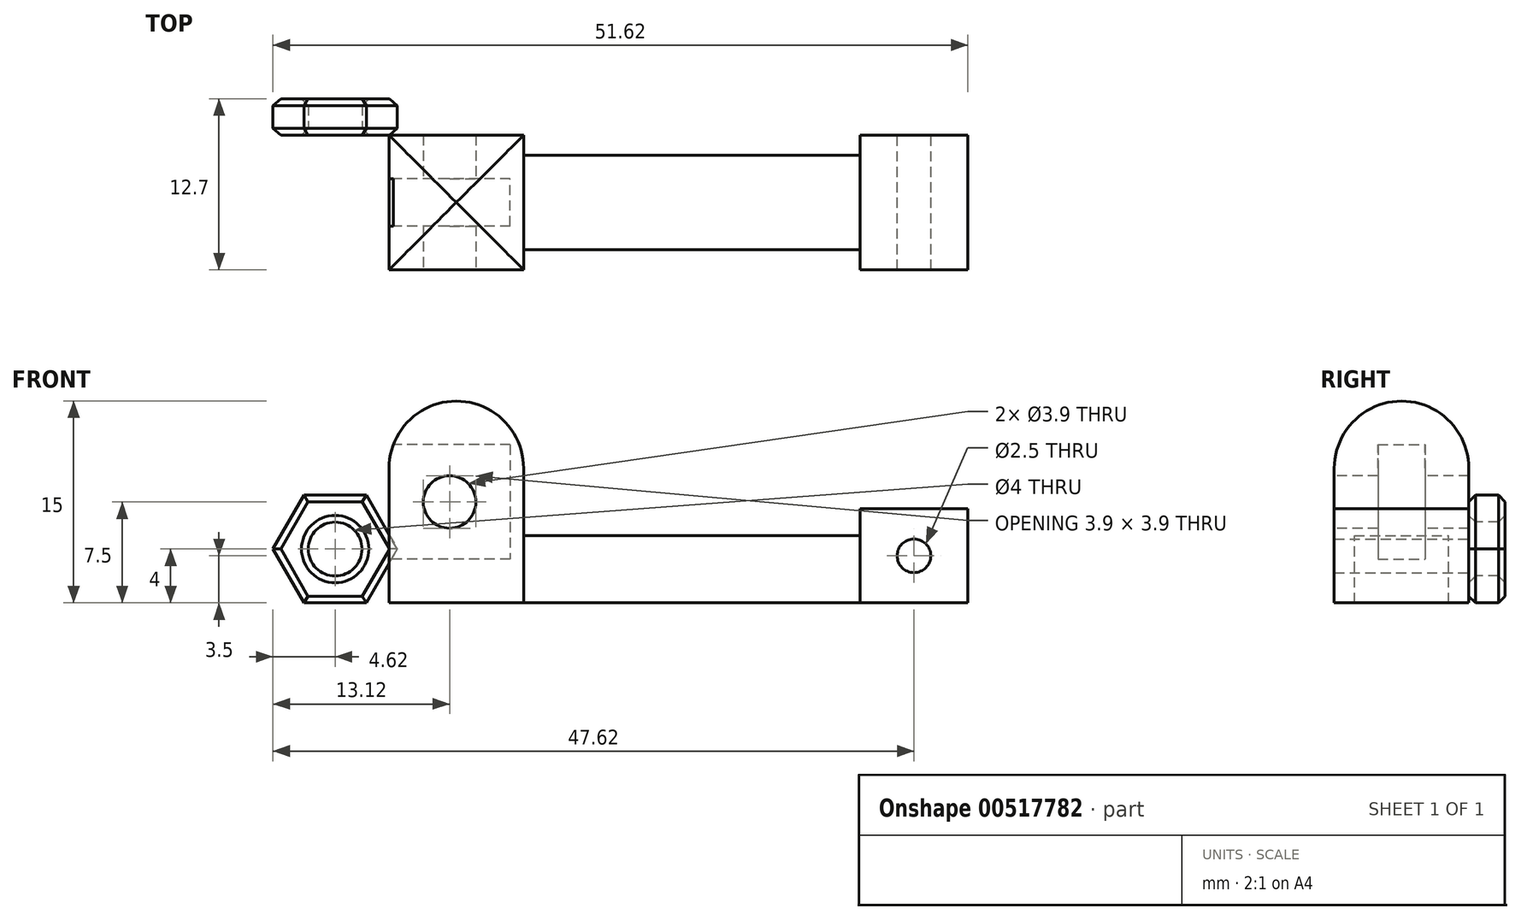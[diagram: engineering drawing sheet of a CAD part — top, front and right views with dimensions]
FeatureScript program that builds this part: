
annotation { "Feature Type Name" : "Feature", "Feature Type Description" : "" }
export const myFeature = defineFeature(function(context is Context, id is Id, definition is map)
    precondition{}
    {
        {
            var Q0;
            Q0=qCreatedBy(makeId("Front.planeOp"),FACE);
            var sketch = newSketch(context, id + "F0", { "sketchPlane" : qUnion([Q0])});
            skLineSegment(sketch, "E0.top", {"start": v(0, 15) * mm, "end": v(10, 15) * mm});
            skLineSegment(sketch, "E0.left", {"start": v(0, 0) * mm, "end": v(0, 15) * mm});
            skLineSegment(sketch, "E0.right", {"start": v(10, 5) * mm, "end": v(10, 15) * mm});
            skLineSegment(sketch, "E1.bottom", {"start": v(0, 0) * mm, "end": v(43, 0) * mm});
            skLineSegment(sketch, "E1.top", {"start": v(10, 5) * mm, "end": v(35, 5) * mm});
            skCircle(sketch, "E2", {"center": v(39, 3.5) * mm, "radius": 1.25 * mm});
            skPoint(sketch, "E3", {"position": v(35, 5) * mm});
            skLineSegment(sketch, "E4", {"start": v(35, 5) * mm, "end": v(35, 7) * mm});
            skLineSegment(sketch, "E5", {"start": v(35, 7) * mm, "end": v(43, 7) * mm});
            skLineSegment(sketch, "E6", {"start": v(43, 7) * mm, "end": v(43, 0) * mm});
            skSolve(sketch);
        }
        {
            var Q0;
            Q0 = qSketchRegion(id + "F0", true);
            extrude(context, id + "F1", {"entities" : qUnion([Q0]), "depth" : 10 * mm, "offsetDistance" : 25 * mm});
        }
        {
            var Q0;
            Q0=makeQuery(id+"F1.opExtrude","SWEPT_FACE",FACE,{"disambiguationData":[OSD([sQuery(id+"F0.wireOp",EDGE,"E0.left")])]});
            var sketch = newSketch(context, id + "F2", { "sketchPlane" : qUnion([Q0])});
            skLineSegment(sketch, "E7.bottom", {"start": v(6.75, 11.75) * mm, "end": v(3.25, 11.75) * mm});
            skLineSegment(sketch, "E7.top", {"start": v(6.75, 3.25) * mm, "end": v(3.25, 3.25) * mm});
            skLineSegment(sketch, "E7.left", {"start": v(6.75, 11.75) * mm, "end": v(6.75, 3.25) * mm});
            skLineSegment(sketch, "E7.right", {"start": v(3.25, 11.75) * mm, "end": v(3.25, 3.25) * mm});
            skPoint(sketch, "E7.middle", {"position": v(5, 7.5) * mm});
            skPoint(sketch, "E7.middle.positionSnap0", {"position": v(0, 7.5) * mm});
            skPoint(sketch, "E7.centerSnap0", {"position": v(0, 7.5) * mm});
            skSolve(sketch);
        }
        {
            var Q0;
            Q0 = qSketchRegion(id + "F2", true);
            extrude(context, id + "F3", {"entities" : qUnion([Q0]), "operationType" : NewBodyOperationType.REMOVE, "oppositeDirection" : true, "depth" : 9 * mm, "offsetDistance" : 25 * mm});
        }
        {
            var Q0;
            Q0=makeQuery(id+"F1.opExtrude","CAP_FACE",FACE,{"disambiguationData":[OSD([sQuery(id+"F0.wireOp",EDGE,"E0.top"),sQuery(id+"F0.wireOp",EDGE,"E0.left"),sQuery(id+"F0.wireOp",EDGE,"E0.right"),sQuery(id+"F0.wireOp",EDGE,"E1.bottom"),sQuery(id+"F0.wireOp",EDGE,"E1.top"),sQuery(id+"F0.wireOp",EDGE,"E1.right")])],"isStart":false});
            var sketch = newSketch(context, id + "F4", { "sketchPlane" : qUnion([Q0])});
            skCircle(sketch, "E8", {"center": v(4.5, 7.5) * mm, "radius": 1.95 * mm});
            skPoint(sketch, "E8.centerSnap0", {"position": v(0, 7.5) * mm});
            skSolve(sketch);
        }
        {
            var Q0;
            Q0 = qSketchRegion(id + "F4", true);
            var Q1;
            Q1=makeQuery(id+"F1.opExtrude","CAP_FACE",FACE,{"disambiguationData":[OSD([sQuery(id+"F0.wireOp",EDGE,"E0.top"),sQuery(id+"F0.wireOp",EDGE,"E0.left"),sQuery(id+"F0.wireOp",EDGE,"E0.right"),sQuery(id+"F0.wireOp",EDGE,"E1.bottom"),sQuery(id+"F0.wireOp",EDGE,"E1.top"),sQuery(id+"F0.wireOp",EDGE,"E1.right")])],"isStart":true});
            extrude(context, id + "F5", {"entities" : qUnion([Q0]), "operationType" : NewBodyOperationType.REMOVE, "endBound" : BoundingType.UP_TO_SURFACE, "oppositeDirection" : true, "depth" : 25 * mm, "endBoundEntityFace" : qUnion([Q1]), "offsetDistance" : 25 * mm});
        }
        {
            var Q0;
            Q0=makeQuery(id+"F1.opExtrude","SWEPT_FACE",FACE,{"disambiguationData":[OSD([sQuery(id+"F0.wireOp",EDGE,"E0.top")])]});
            fillet(context, id + "F6", {"entities" : qUnion([Q0]), "radius" : 5 * mm, "tangentPropagation" : true, "allowEdgeOverflow" : false});
        }
        {
            var Q0;
            Q0=makeQuery(id+"F1.opExtrude","SWEPT_FACE",FACE,{"disambiguationData":[OSD([sQuery(id+"F0.wireOp",EDGE,"E1.top")])]});
            var sketch = newSketch(context, id + "F7", { "sketchPlane" : qUnion([Q0])});
            skLineSegment(sketch, "E9.bottom", {"start": v(35, 0) * mm, "end": v(10, 0) * mm});
            skLineSegment(sketch, "E9.top", {"start": v(35, -1.5) * mm, "end": v(10, -1.5) * mm});
            skLineSegment(sketch, "E9.left", {"start": v(35, 0) * mm, "end": v(35, -1.5) * mm});
            skLineSegment(sketch, "E9.right", {"start": v(10, 0) * mm, "end": v(10, -1.5) * mm});
            skLineSegment(sketch, "E10.bottom", {"start": v(10, -10) * mm, "end": v(10, -10) * mm});
            skLineSegment(sketch, "E10.top", {"start": v(35, -8.5) * mm, "end": v(10, -8.5) * mm});
            skLineSegment(sketch, "E10.left", {"start": v(35, -10) * mm, "end": v(35, -8.5) * mm});
            skLineSegment(sketch, "E10.right", {"start": v(10, -10) * mm, "end": v(10, -8.5) * mm});
            skSolve(sketch);
        }
        {
            var Q0;
            Q0=makeQuery(id+"F7.imprint","IMPRINT",FACE,{"disambiguationData":[TD([[makeQuery(id+"F7.imprint","IMPRINT",EDGE,{"derivedFrom":sQuery(id+"F7.wireOp",EDGE,"E9.bottom")}),-1.0]])]});
            var Q1;
            Q1=makeQuery(id+"F7.imprint","IMPRINT",FACE,{"disambiguationData":[TD([[makeQuery(id+"F7.imprint","IMPRINT",EDGE,{"derivedFrom":sQuery(id+"F7.wireOp",EDGE,"E10.top")}),1.0]])]});
            var Q2;
            Q2=makeQuery(id+"F1.opExtrude","SWEPT_FACE",FACE,{"disambiguationData":[OSD([sQuery(id+"F0.wireOp",EDGE,"E1.bottom")])]});
            extrude(context, id + "F8", {"entities" : qUnion([Q0, Q1]), "operationType" : NewBodyOperationType.REMOVE, "endBound" : BoundingType.UP_TO_SURFACE, "oppositeDirection" : true, "depth" : 25 * mm, "endBoundEntityFace" : qUnion([Q2]), "offsetDistance" : 25 * mm});
        }
        {
            var Q0;
            Q0=qCreatedBy(makeId("Front.planeOp"),FACE);
            var sketch = newSketch(context, id + "F9", { "sketchPlane" : qUnion([Q0])});
            skCircle(sketch, "E11", {"center": v(-4, 4) * mm, "radius": 2 * mm});
            skCircle(sketch, "E12.cCircle", {"center": v(-4, 4) * mm, "radius": 4 * mm, "construction": true});
            skLineSegment(sketch, "E12.0", {"start": v(-6.3, 0) * mm, "end": v(-8.62, 4) * mm});
            skLineSegment(sketch, "E12.1", {"start": v(-8.62, 4) * mm, "end": v(-6.3, 8) * mm});
            skLineSegment(sketch, "E12.2", {"start": v(-6.3, 8) * mm, "end": v(-1.7, 8) * mm});
            skLineSegment(sketch, "E12.3", {"start": v(-1.7, 8) * mm, "end": v(0.62, 4) * mm});
            skLineSegment(sketch, "E12.4", {"start": v(0.62, 4) * mm, "end": v(-1.7, 0) * mm});
            skLineSegment(sketch, "E12.5", {"start": v(-1.7, 0) * mm, "end": v(-6.3, 0) * mm});
            skPoint(sketch, "E12.0.midPoint", {"position": v(-7.46, 2) * mm});
            skLineSegment(sketch, "E13", {"start": v(26.6, 21.08) * mm, "end": v(-14.67, 21.08) * mm, "construction": true});
            skSolve(sketch);
        }
        {
            var Q0;
            Q0 = qSketchRegion(id + "F9", true);
            extrude(context, id + "F10", {"entities" : qUnion([Q0]), "oppositeDirection" : true, "depth" : 2.7 * mm, "offsetDistance" : 25 * mm});
        }
        {
            var Q0;
            Q0=makeQuery(id+"F10.opExtrude","CAP_FACE",FACE,{"disambiguationData":[OSD([sQuery(id+"F9.wireOp",EDGE,"E11"),sQuery(id+"F9.wireOp",EDGE,"E12.0"),sQuery(id+"F9.wireOp",EDGE,"E12.1"),sQuery(id+"F9.wireOp",EDGE,"E12.2"),sQuery(id+"F9.wireOp",EDGE,"E12.3"),sQuery(id+"F9.wireOp",EDGE,"E12.4"),sQuery(id+"F9.wireOp",EDGE,"E12.5")])],"isStart":false});
            var Q1;
            Q1=makeQuery(id+"F10.opExtrude","CAP_FACE",FACE,{"disambiguationData":[OSD([sQuery(id+"F9.wireOp",EDGE,"E11"),sQuery(id+"F9.wireOp",EDGE,"E12.0"),sQuery(id+"F9.wireOp",EDGE,"E12.1"),sQuery(id+"F9.wireOp",EDGE,"E12.2"),sQuery(id+"F9.wireOp",EDGE,"E12.3"),sQuery(id+"F9.wireOp",EDGE,"E12.4"),sQuery(id+"F9.wireOp",EDGE,"E12.5")])],"isStart":true});
            chamfer(context, id + "F11", {"entities" : qUnion([Q0, Q1]), "width" : .5 * mm, "tangentPropagation" : true});
        }
    });
